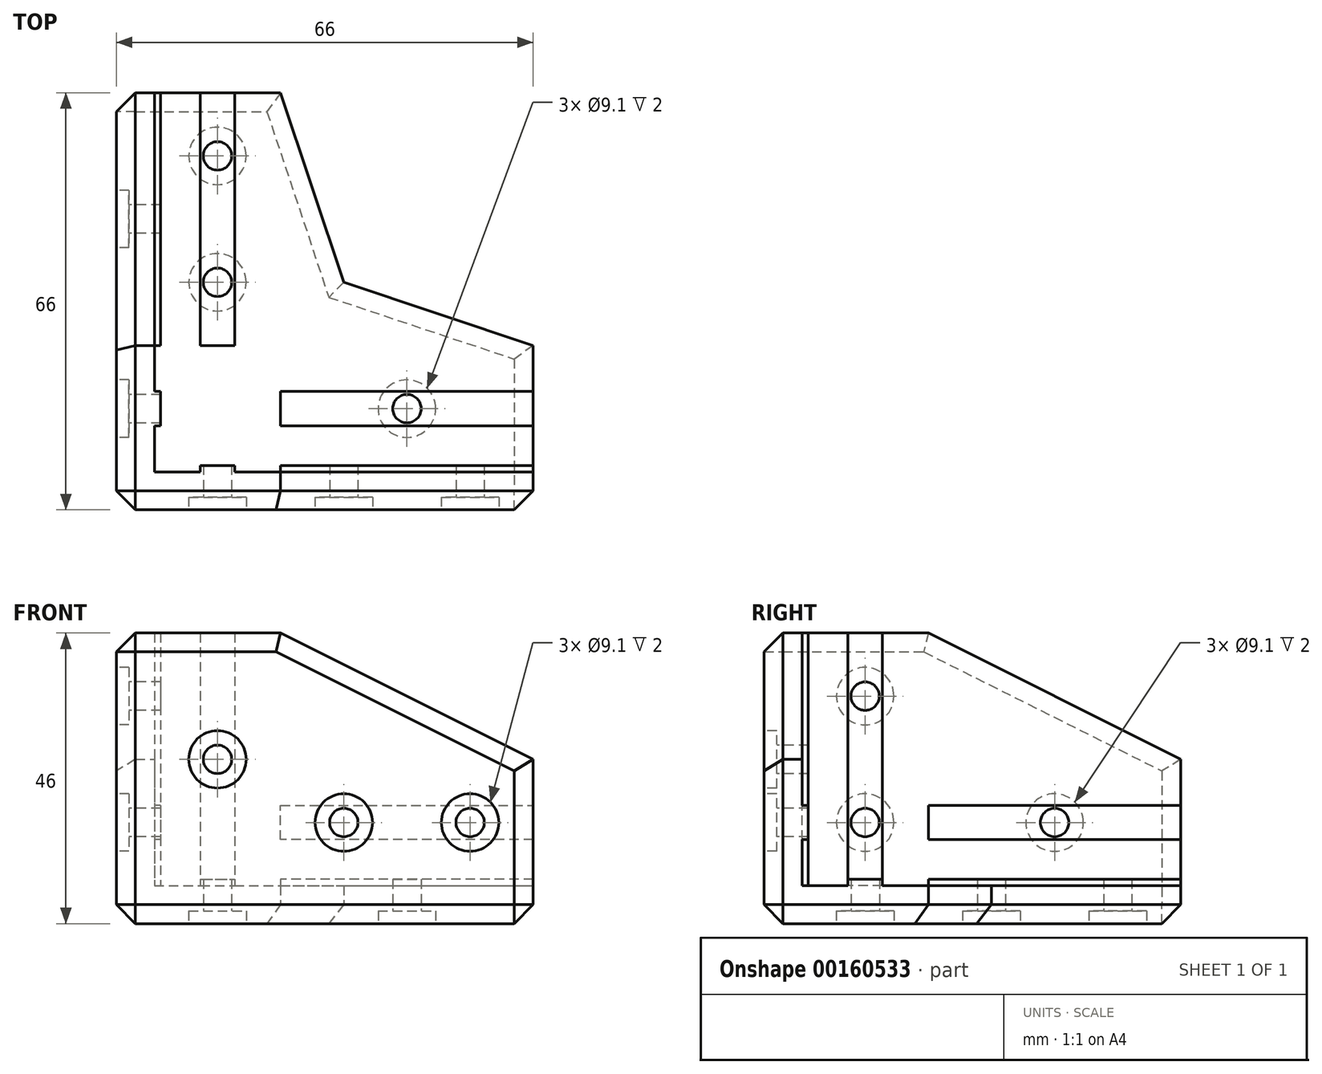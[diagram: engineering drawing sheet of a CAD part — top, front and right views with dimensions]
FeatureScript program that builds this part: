
annotation { "Feature Type Name" : "Feature", "Feature Type Description" : "" }
export const myFeature = defineFeature(function(context is Context, id is Id, definition is map)
    precondition{}
    {
        {
            var Q0;
            Q0=qCreatedBy(makeId("Top.planeOp"),FACE);
            var sketch = newSketch(context, id + "F0", { "sketchPlane" : qUnion([Q0])});
            skLineSegment(sketch, "E0", {"start": v(0, 0) * mm, "end": v(0, 66) * mm});
            skLineSegment(sketch, "E1", {"start": v(0, 66) * mm, "end": v(26, 66) * mm});
            skLineSegment(sketch, "E2", {"start": v(26, 66) * mm, "end": v(26, 26) * mm});
            skLineSegment(sketch, "E3", {"start": v(26, 26) * mm, "end": v(66, 26) * mm});
            skLineSegment(sketch, "E4", {"start": v(66, 26) * mm, "end": v(66, 0) * mm});
            skLineSegment(sketch, "E5", {"start": v(66, 0) * mm, "end": v(0, 0) * mm});
            skLineSegment(sketch, "E6", {"start": v(66, 6) * mm, "end": v(6, 6) * mm, "construction": true});
            skLineSegment(sketch, "E7", {"start": v(6, 6) * mm, "end": v(6, 66) * mm, "construction": true});
            skSolve(sketch);
        }
        {
            var Q0;
            Q0=qSketchRegion(id+"F0",true);
            extrude(context, id + "F1", {"entities" : qUnion([Q0]), "depth" : 6 * mm});
        }
        {
            var Q0;
            Q0=makeQuery(id+"F1.opExtrude","CAP_FACE",FACE,{"disambiguationData":[OSD([sQuery(id+"F0.wireOp",EDGE,"E0"),sQuery(id+"F0.wireOp",EDGE,"E1"),sQuery(id+"F0.wireOp",EDGE,"E2"),sQuery(id+"F0.wireOp",EDGE,"E3"),sQuery(id+"F0.wireOp",EDGE,"E4"),sQuery(id+"F0.wireOp",EDGE,"E5")])],"isStart":false});
            var sketch = newSketch(context, id + "F2", { "sketchPlane" : qUnion([Q0])});
            skLineSegment(sketch, "E8", {"start": v(0, 66) * mm, "end": v(6, 66) * mm});
            skLineSegment(sketch, "E9", {"start": v(6, 66) * mm, "end": v(6, 6) * mm});
            skLineSegment(sketch, "E10", {"start": v(6, 6) * mm, "end": v(66, 6) * mm});
            skLineSegment(sketch, "E11", {"start": v(66, 6) * mm, "end": v(66, 0) * mm});
            skLineSegment(sketch, "E12", {"start": v(66, 0) * mm, "end": v(0, 0) * mm});
            skLineSegment(sketch, "E13", {"start": v(0, 0) * mm, "end": v(0, 66) * mm});
            skSolve(sketch);
        }
        {
            var Q0;
            Q0=makeQuery(id+"F2.imprint","IMPRINT",FACE,{"disambiguationData":[TD([[makeQuery(id+"F2.imprint","IMPRINT",EDGE,{"derivedFrom":sQuery(id+"F2.wireOp",EDGE,"E8")}),-1.0]])]});
            extrude(context, id + "F3", {"entities" : qUnion([Q0]), "operationType" : NewBodyOperationType.ADD, "depth" : 20 * mm});
        }
        {
            var Q0;
            Q0=makeQuery(id+"F3.opExtrude","CAP_FACE",FACE,{"disambiguationData":[OSD([sQuery(id+"F2.wireOp",EDGE,"E8"),sQuery(id+"F2.wireOp",EDGE,"E9"),sQuery(id+"F2.wireOp",EDGE,"E10"),sQuery(id+"F2.wireOp",EDGE,"E11"),sQuery(id+"F2.wireOp",EDGE,"E12"),sQuery(id+"F2.wireOp",EDGE,"E13")])],"isStart":false});
            var sketch = newSketch(context, id + "F4", { "sketchPlane" : qUnion([Q0])});
            skLineSegment(sketch, "E14", {"start": v(6, 26) * mm, "end": v(0, 26) * mm});
            skLineSegment(sketch, "E15", {"start": v(0, 26) * mm, "end": v(0, 0) * mm});
            skLineSegment(sketch, "E16", {"start": v(0, 0) * mm, "end": v(26, 0) * mm});
            skLineSegment(sketch, "E17", {"start": v(26, 0) * mm, "end": v(26, 6) * mm});
            skLineSegment(sketch, "E18", {"start": v(26, 6) * mm, "end": v(6, 6) * mm});
            skLineSegment(sketch, "E19", {"start": v(6, 6) * mm, "end": v(6, 26) * mm});
            skSolve(sketch);
        }
        {
            var Q0;
            Q0=qSketchRegion(id+"F4",true);
            extrude(context, id + "F5", {"entities" : qUnion([Q0]), "operationType" : NewBodyOperationType.ADD, "depth" : 20 * mm});
        }
        {
            var Q0;
            Q0=makeQuery(id+"F1.opExtrude","CAP_FACE",FACE,{"disambiguationData":[OSD([sQuery(id+"F0.wireOp",EDGE,"E0"),sQuery(id+"F0.wireOp",EDGE,"E1"),sQuery(id+"F0.wireOp",EDGE,"E2"),sQuery(id+"F0.wireOp",EDGE,"E3"),sQuery(id+"F0.wireOp",EDGE,"E4"),sQuery(id+"F0.wireOp",EDGE,"E5")])],"isStart":false});
            var sketch = newSketch(context, id + "F6", { "sketchPlane" : qUnion([Q0])});
            skLineSegment(sketch, "E20", {"start": v(66, 16) * mm, "end": v(6, 16) * mm, "construction": true});
            skLineSegment(sketch, "E21", {"start": v(16, 66) * mm, "end": v(16, 6) * mm, "construction": true});
            skLineSegment(sketch, "E22", {"start": v(16, 6) * mm, "end": v(18.71, 6) * mm});
            skLineSegment(sketch, "E23", {"start": v(18.71, 6) * mm, "end": v(18.71, 7) * mm});
            skLineSegment(sketch, "E24", {"start": v(18.71, 7) * mm, "end": v(13.3, 7) * mm});
            skLineSegment(sketch, "E25", {"start": v(13.3, 7) * mm, "end": v(13.3, 6) * mm});
            skLineSegment(sketch, "E26", {"start": v(13.3, 6) * mm, "end": v(16, 6) * mm});
            skLineSegment(sketch, "E27", {"start": v(6, 16) * mm, "end": v(6, 18.7) * mm});
            skLineSegment(sketch, "E28", {"start": v(6, 18.7) * mm, "end": v(7, 18.7) * mm});
            skLineSegment(sketch, "E29", {"start": v(7, 18.7) * mm, "end": v(7, 13.29) * mm});
            skLineSegment(sketch, "E30", {"start": v(7, 13.29) * mm, "end": v(6, 13.29) * mm});
            skLineSegment(sketch, "E31", {"start": v(6, 13.29) * mm, "end": v(6, 16) * mm});
            skSolve(sketch);
        }
        {
            var Q0;
            Q0=qSketchRegion(id+"F6",true);
            extrude(context, id + "F7", {"entities" : qUnion([Q0]), "operationType" : NewBodyOperationType.ADD, "depth" : 40 * mm});
        }
        {
            var Q0;
            Q0=makeQuery(id+"F1.opExtrude","CAP_FACE",FACE,{"disambiguationData":[OSD([sQuery(id+"F0.wireOp",EDGE,"E0"),sQuery(id+"F0.wireOp",EDGE,"E1"),sQuery(id+"F0.wireOp",EDGE,"E2"),sQuery(id+"F0.wireOp",EDGE,"E3"),sQuery(id+"F0.wireOp",EDGE,"E4"),sQuery(id+"F0.wireOp",EDGE,"E5")])],"isStart":false});
            var sketch = newSketch(context, id + "F8", { "sketchPlane" : qUnion([Q0])});
            skLineSegment(sketch, "E32", {"start": v(66, 16) * mm, "end": v(7, 16) * mm, "construction": true});
            skLineSegment(sketch, "E33", {"start": v(66, 16) * mm, "end": v(66, 18.7) * mm});
            skLineSegment(sketch, "E34", {"start": v(66, 18.7) * mm, "end": v(26, 18.7) * mm});
            skLineSegment(sketch, "E35", {"start": v(26, 18.7) * mm, "end": v(26, 13.29) * mm});
            skLineSegment(sketch, "E36", {"start": v(26, 13.29) * mm, "end": v(66, 13.29) * mm});
            skLineSegment(sketch, "E37", {"start": v(66, 13.29) * mm, "end": v(66, 16) * mm});
            skLineSegment(sketch, "E38", {"start": v(16, 66) * mm, "end": v(16, 7) * mm, "construction": true});
            skLineSegment(sketch, "E39", {"start": v(16, 66) * mm, "end": v(13.3, 66) * mm});
            skLineSegment(sketch, "E40", {"start": v(13.3, 66) * mm, "end": v(13.3, 26) * mm});
            skLineSegment(sketch, "E41", {"start": v(13.3, 26) * mm, "end": v(18.7, 26) * mm});
            skLineSegment(sketch, "E42", {"start": v(18.7, 26) * mm, "end": v(18.7, 66) * mm});
            skLineSegment(sketch, "E43", {"start": v(18.7, 66) * mm, "end": v(16, 66) * mm});
            skSolve(sketch);
        }
        {
            var Q0;
            Q0=qSketchRegion(id+"F8",true);
            extrude(context, id + "F9", {"entities" : qUnion([Q0]), "operationType" : NewBodyOperationType.ADD, "flatOperationType" : FlatOperationType.REMOVE, "offsetDistance" : 25 * mm, "depth" : 1 * mm, "domain" : OperationDomain.MODEL});
        }
        {
            var Q0;
            {var subQ1=sQuery(id+"F2.wireOp",EDGE,"E10");var subQ2=sQuery(id+"F0.wireOp",EDGE,"E4");var subQ3=sQuery(id+"F4.wireOp",EDGE,"E18");Q0=makeQuery(id+"F7.boolean.opBoolean","SPLIT",FACE,{"disambiguationData":[TD([makeQuery(id+"F1.opExtrude","SWEPT_FACE",FACE,{"disambiguationData":[OSD([subQ2])]})])],"derivedFrom":makeQuery(id+"F5.boolean.opBoolean","MERGE",FACE,{"derivedFrom":[makeQuery(id+"F3.opExtrude","SWEPT_FACE",FACE,{"disambiguationData":[OSD([subQ1])]}),makeQuery(id+"F5.opExtrude","SWEPT_FACE",FACE,{"disambiguationData":[OSD([subQ3])]})]})});}
            var sketch = newSketch(context, id + "F10", { "sketchPlane" : qUnion([Q0])});
            skLineSegment(sketch, "E44", {"start": v(-66, 16) * mm, "end": v(-26, 16) * mm, "construction": true});
            skLineSegment(sketch, "E45", {"start": v(-66, 16) * mm, "end": v(-66, 13.3) * mm});
            skLineSegment(sketch, "E46", {"start": v(-66, 13.3) * mm, "end": v(-26, 13.3) * mm});
            skLineSegment(sketch, "E47", {"start": v(-26, 13.3) * mm, "end": v(-26, 16) * mm});
            skLineSegment(sketch, "E48", {"start": v(-26, 18.71) * mm, "end": v(-66, 18.71) * mm});
            skLineSegment(sketch, "E49", {"start": v(-66, 18.71) * mm, "end": v(-66, 16) * mm});
            skLineSegment(sketch, "E50", {"start": v(-26, 18.71) * mm, "end": v(-26, 16) * mm});
            skSolve(sketch);
        }
        {
            var Q0;
            Q0=qSketchRegion(id+"F10",true);
            extrude(context, id + "F11", {"entities" : qUnion([Q0]), "operationType" : NewBodyOperationType.ADD, "flatOperationType" : FlatOperationType.REMOVE, "offsetDistance" : 25 * mm, "depth" : 1 * mm, "domain" : OperationDomain.MODEL});
        }
        {
            var Q0;
            {var subQ0=sQuery(id+"F2.wireOp",EDGE,"E9");var subQ3=sQuery(id+"F0.wireOp",EDGE,"E1");var subQ5=sQuery(id+"F4.wireOp",EDGE,"E19");Q0=makeQuery(id+"F7.boolean.opBoolean","SPLIT",FACE,{"disambiguationData":[TD([makeQuery(id+"F1.opExtrude","SWEPT_FACE",FACE,{"disambiguationData":[OSD([subQ3])]})])],"derivedFrom":makeQuery(id+"F5.boolean.opBoolean","MERGE",FACE,{"derivedFrom":[makeQuery(id+"F3.opExtrude","SWEPT_FACE",FACE,{"disambiguationData":[OSD([subQ0])]}),makeQuery(id+"F5.opExtrude","SWEPT_FACE",FACE,{"disambiguationData":[OSD([subQ5])]})]})});}
            var sketch = newSketch(context, id + "F12", { "sketchPlane" : qUnion([Q0])});
            skLineSegment(sketch, "E51", {"start": v(66, 16) * mm, "end": v(26, 16) * mm, "construction": true});
            skLineSegment(sketch, "E52", {"start": v(66, 16) * mm, "end": v(66, 18.71) * mm});
            skLineSegment(sketch, "E53", {"start": v(66, 18.71) * mm, "end": v(26, 18.7) * mm});
            skLineSegment(sketch, "E54", {"start": v(26, 18.7) * mm, "end": v(26, 13.29) * mm});
            skLineSegment(sketch, "E55", {"start": v(26, 13.29) * mm, "end": v(66, 13.29) * mm});
            skLineSegment(sketch, "E56", {"start": v(66, 16) * mm, "end": v(66, 13.29) * mm});
            skSolve(sketch);
        }
        {
            var Q0;
            Q0=qSketchRegion(id+"F12",true);
            extrude(context, id + "F13", {"entities" : qUnion([Q0]), "operationType" : NewBodyOperationType.ADD, "flatOperationType" : FlatOperationType.REMOVE, "offsetDistance" : 25 * mm, "depth" : 1 * mm, "domain" : OperationDomain.MODEL});
        }
        {
            var Q0;
            Q0=makeQuery(id+"F5.boolean.opBoolean","MERGE",FACE,{"derivedFrom":[makeQuery(id+"F3.boolean.opBoolean","MERGE",FACE,{"derivedFrom":[makeQuery(id+"F1.opExtrude","SWEPT_FACE",FACE,{"disambiguationData":[OSD([sQuery(id+"F0.wireOp",EDGE,"E5")])]}),makeQuery(id+"F3.opExtrude","SWEPT_FACE",FACE,{"disambiguationData":[OSD([sQuery(id+"F2.wireOp",EDGE,"E12")])]})]}),makeQuery(id+"F5.opExtrude","SWEPT_FACE",FACE,{"disambiguationData":[OSD([sQuery(id+"F4.wireOp",EDGE,"E16")])]})]});
            var sketch = newSketch(context, id + "F14", { "sketchPlane" : qUnion([Q0])});
            skLineSegment(sketch, "E57", {"start": v(6, 46) * mm, "end": v(6, 6) * mm, "construction": true});
            skLineSegment(sketch, "E58", {"start": v(6, 6) * mm, "end": v(66, 6) * mm, "construction": true});
            skCircle(sketch, "E59", {"center": v(56, 16) * mm, "radius": 2.25 * mm});
            skCircle(sketch, "E60", {"center": v(36, 16) * mm, "radius": 2.25 * mm});
            skCircle(sketch, "E61", {"center": v(16, 26) * mm, "radius": 2.25 * mm});
            skLineSegment(sketch, "E62", {"start": v(26, 26) * mm, "end": v(6, 26) * mm, "construction": true});
            skLineSegment(sketch, "E63", {"start": v(26, 26) * mm, "end": v(26, 6) * mm, "construction": true});
            skSolve(sketch);
        }
        {
            var Q0;
            Q0=makeQuery(id+"F14.imprint","IMPRINT",FACE,{"disambiguationData":[TD([[makeQuery(id+"F14.imprint","IMPRINT",EDGE,{"derivedFrom":sQuery(id+"F14.wireOp",EDGE,"E59")}),1.0]])]});
            var Q1;
            Q1=makeQuery(id+"F14.imprint","IMPRINT",FACE,{"disambiguationData":[TD([[makeQuery(id+"F14.imprint","IMPRINT",EDGE,{"derivedFrom":sQuery(id+"F14.wireOp",EDGE,"E61")}),1.0]])]});
            var Q2;
            Q2=makeQuery(id+"F14.imprint","IMPRINT",FACE,{"disambiguationData":[TD([[makeQuery(id+"F14.imprint","IMPRINT",EDGE,{"derivedFrom":sQuery(id+"F14.wireOp",EDGE,"E60")}),1.0]])]});
            extrude(context, id + "F15", {"entities" : qUnion([Q0, Q1, Q2]), "operationType" : NewBodyOperationType.REMOVE, "endBound" : BoundingType.UP_TO_NEXT, "oppositeDirection" : true, "depth" : 25 * mm});
        }
        {
            var Q0;
            Q0=makeQuery(id+"F5.boolean.opBoolean","MERGE",FACE,{"derivedFrom":[makeQuery(id+"F3.boolean.opBoolean","MERGE",FACE,{"derivedFrom":[makeQuery(id+"F1.opExtrude","SWEPT_FACE",FACE,{"disambiguationData":[OSD([sQuery(id+"F0.wireOp",EDGE,"E0")])]}),makeQuery(id+"F3.opExtrude","SWEPT_FACE",FACE,{"disambiguationData":[OSD([sQuery(id+"F2.wireOp",EDGE,"E13")])]})]}),makeQuery(id+"F5.opExtrude","SWEPT_FACE",FACE,{"disambiguationData":[OSD([sQuery(id+"F4.wireOp",EDGE,"E15")])]})]});
            var sketch = newSketch(context, id + "F16", { "sketchPlane" : qUnion([Q0])});
            skLineSegment(sketch, "E64", {"start": v(-6, 46) * mm, "end": v(-6, 6) * mm, "construction": true});
            skLineSegment(sketch, "E65", {"start": v(-6, 6) * mm, "end": v(-66, 6) * mm, "construction": true});
            skCircle(sketch, "E66", {"center": v(-16, 36) * mm, "radius": 2.25 * mm});
            skCircle(sketch, "E67", {"center": v(-46, 16) * mm, "radius": 2.25 * mm});
            skCircle(sketch, "E68", {"center": v(-16, 16) * mm, "radius": 2.25 * mm});
            skSolve(sketch);
        }
        {
            var Q0;
            Q0=qSketchRegion(id+"F16",true);
            extrude(context, id + "F17", {"entities" : qUnion([Q0]), "operationType" : NewBodyOperationType.REMOVE, "endBound" : BoundingType.UP_TO_NEXT, "oppositeDirection" : true, "depth" : 25 * mm});
        }
        {
            var Q0;
            Q0=makeQuery(id+"F1.opExtrude","CAP_FACE",FACE,{"disambiguationData":[OSD([sQuery(id+"F0.wireOp",EDGE,"E0"),sQuery(id+"F0.wireOp",EDGE,"E1"),sQuery(id+"F0.wireOp",EDGE,"E2"),sQuery(id+"F0.wireOp",EDGE,"E3"),sQuery(id+"F0.wireOp",EDGE,"E4"),sQuery(id+"F0.wireOp",EDGE,"E5")])],"isStart":true});
            var sketch = newSketch(context, id + "F18", { "sketchPlane" : qUnion([Q0])});
            skLineSegment(sketch, "E69", {"start": v(66, -6) * mm, "end": v(6, -6) * mm, "construction": true});
            skLineSegment(sketch, "E70", {"start": v(6, -6) * mm, "end": v(6, -66) * mm, "construction": true});
            skCircle(sketch, "E71", {"center": v(46, -16) * mm, "radius": 2.25 * mm});
            skCircle(sketch, "E72", {"center": v(16, -56) * mm, "radius": 2.25 * mm});
            skCircle(sketch, "E73", {"center": v(16, -36) * mm, "radius": 2.25 * mm});
            skSolve(sketch);
        }
        {
            var Q0;
            Q0=qSketchRegion(id+"F18",true);
            extrude(context, id + "F19", {"entities" : qUnion([Q0]), "operationType" : NewBodyOperationType.REMOVE, "endBound" : BoundingType.UP_TO_NEXT, "oppositeDirection" : true, "depth" : 25 * mm});
        }
        {
            var Q0;
            Q0=makeQuery(id+"F5.boolean.opBoolean","MERGE",FACE,{"derivedFrom":[makeQuery(id+"F3.boolean.opBoolean","MERGE",FACE,{"derivedFrom":[makeQuery(id+"F1.opExtrude","SWEPT_FACE",FACE,{"disambiguationData":[OSD([sQuery(id+"F0.wireOp",EDGE,"E5")])]}),makeQuery(id+"F3.opExtrude","SWEPT_FACE",FACE,{"disambiguationData":[OSD([sQuery(id+"F2.wireOp",EDGE,"E12")])]})]}),makeQuery(id+"F5.opExtrude","SWEPT_FACE",FACE,{"disambiguationData":[OSD([sQuery(id+"F4.wireOp",EDGE,"E16")])]})]});
            var sketch = newSketch(context, id + "F20", { "sketchPlane" : qUnion([Q0])});
            skCircle(sketch, "E74", {"center": v(16, 26) * mm, "radius": 4.55 * mm});
            skCircle(sketch, "E75", {"center": v(36, 16) * mm, "radius": 4.55 * mm});
            skCircle(sketch, "E76", {"center": v(56, 16) * mm, "radius": 4.55 * mm});
            skSolve(sketch);
        }
        {
            var Q0;
            Q0=qSketchRegion(id+"F20",true);
            extrude(context, id + "F21", {"entities" : qUnion([Q0]), "operationType" : NewBodyOperationType.REMOVE, "oppositeDirection" : true, "depth" : 2 * mm});
        }
        {
            var Q0;
            Q0=makeQuery(id+"F5.boolean.opBoolean","MERGE",FACE,{"derivedFrom":[makeQuery(id+"F3.boolean.opBoolean","MERGE",FACE,{"derivedFrom":[makeQuery(id+"F1.opExtrude","SWEPT_FACE",FACE,{"disambiguationData":[OSD([sQuery(id+"F0.wireOp",EDGE,"E0")])]}),makeQuery(id+"F3.opExtrude","SWEPT_FACE",FACE,{"disambiguationData":[OSD([sQuery(id+"F2.wireOp",EDGE,"E13")])]})]}),makeQuery(id+"F5.opExtrude","SWEPT_FACE",FACE,{"disambiguationData":[OSD([sQuery(id+"F4.wireOp",EDGE,"E15")])]})]});
            var sketch = newSketch(context, id + "F22", { "sketchPlane" : qUnion([Q0])});
            skCircle(sketch, "E77", {"center": v(-16, 36) * mm, "radius": 4.55 * mm});
            skCircle(sketch, "E78", {"center": v(-46, 16) * mm, "radius": 4.55 * mm});
            skCircle(sketch, "E79", {"center": v(-16, 16) * mm, "radius": 4.55 * mm});
            skSolve(sketch);
        }
        {
            var Q0;
            Q0=qSketchRegion(id+"F22",true);
            extrude(context, id + "F23", {"entities" : qUnion([Q0]), "operationType" : NewBodyOperationType.REMOVE, "oppositeDirection" : true, "depth" : 2 * mm});
        }
        {
            var Q0;
            Q0=makeQuery(id+"F1.opExtrude","CAP_FACE",FACE,{"disambiguationData":[OSD([sQuery(id+"F0.wireOp",EDGE,"E0"),sQuery(id+"F0.wireOp",EDGE,"E1"),sQuery(id+"F0.wireOp",EDGE,"E2"),sQuery(id+"F0.wireOp",EDGE,"E3"),sQuery(id+"F0.wireOp",EDGE,"E4"),sQuery(id+"F0.wireOp",EDGE,"E5")])],"isStart":true});
            var sketch = newSketch(context, id + "F24", { "sketchPlane" : qUnion([Q0])});
            skCircle(sketch, "E80", {"center": v(16, -56) * mm, "radius": 4.55 * mm});
            skCircle(sketch, "E81", {"center": v(46, -16) * mm, "radius": 4.55 * mm});
            skCircle(sketch, "E82", {"center": v(16, -36) * mm, "radius": 4.55 * mm});
            skSolve(sketch);
        }
        {
            var Q0;
            Q0=qSketchRegion(id+"F24",true);
            extrude(context, id + "F25", {"entities" : qUnion([Q0]), "operationType" : NewBodyOperationType.REMOVE, "oppositeDirection" : true, "depth" : 2 * mm});
        }
        {
            var Q0;
            Q0=makeQuery(id+"F5.boolean.opBoolean","MERGE",FACE,{"derivedFrom":[makeQuery(id+"F3.boolean.opBoolean","MERGE",FACE,{"derivedFrom":[makeQuery(id+"F1.opExtrude","SWEPT_FACE",FACE,{"disambiguationData":[OSD([sQuery(id+"F0.wireOp",EDGE,"E5")])]}),makeQuery(id+"F3.opExtrude","SWEPT_FACE",FACE,{"disambiguationData":[OSD([sQuery(id+"F2.wireOp",EDGE,"E12")])]})]}),makeQuery(id+"F5.opExtrude","SWEPT_FACE",FACE,{"disambiguationData":[OSD([sQuery(id+"F4.wireOp",EDGE,"E16")])]})]});
            var sketch = newSketch(context, id + "F26", { "sketchPlane" : qUnion([Q0])});
            skLineSegment(sketch, "E83", {"start": v(26, 46) * mm, "end": v(26, 26) * mm});
            skLineSegment(sketch, "E84", {"start": v(26, 26) * mm, "end": v(66, 26) * mm});
            skLineSegment(sketch, "E85", {"start": v(66, 26) * mm, "end": v(26, 46) * mm});
            skSolve(sketch);
        }
        {
            var Q0;
            Q0 = qSketchRegion(id + "F26", true);
            extrude(context, id + "F27", {"entities" : qUnion([Q0]), "operationType" : NewBodyOperationType.ADD, "oppositeDirection" : true, "depth" : 6 * mm});
        }
        {
            var Q0;
            Q0=makeQuery(id+"F5.boolean.opBoolean","MERGE",FACE,{"derivedFrom":[makeQuery(id+"F3.boolean.opBoolean","MERGE",FACE,{"derivedFrom":[makeQuery(id+"F1.opExtrude","SWEPT_FACE",FACE,{"disambiguationData":[OSD([sQuery(id+"F0.wireOp",EDGE,"E0")])]}),makeQuery(id+"F3.opExtrude","SWEPT_FACE",FACE,{"disambiguationData":[OSD([sQuery(id+"F2.wireOp",EDGE,"E13")])]})]}),makeQuery(id+"F5.opExtrude","SWEPT_FACE",FACE,{"disambiguationData":[OSD([sQuery(id+"F4.wireOp",EDGE,"E15")])]})]});
            var sketch = newSketch(context, id + "F28", { "sketchPlane" : qUnion([Q0])});
            skLineSegment(sketch, "E86", {"start": v(-66, 26) * mm, "end": v(-26, 26) * mm});
            skLineSegment(sketch, "E87", {"start": v(-26, 26) * mm, "end": v(-26, 46) * mm});
            skLineSegment(sketch, "E88", {"start": v(-26, 46) * mm, "end": v(-66, 26) * mm});
            skSolve(sketch);
        }
        {
            var Q0;
            Q0 = qSketchRegion(id + "F28", true);
            extrude(context, id + "F29", {"entities" : qUnion([Q0]), "operationType" : NewBodyOperationType.ADD, "oppositeDirection" : true, "depth" : 6 * mm});
        }
        {
            var Q0;
            Q0=makeQuery(id+"F1.opExtrude","CAP_FACE",FACE,{"disambiguationData":[OSD([sQuery(id+"F0.wireOp",EDGE,"E0"),sQuery(id+"F0.wireOp",EDGE,"E1"),sQuery(id+"F0.wireOp",EDGE,"E2"),sQuery(id+"F0.wireOp",EDGE,"E3"),sQuery(id+"F0.wireOp",EDGE,"E4"),sQuery(id+"F0.wireOp",EDGE,"E5")])],"isStart":true});
            var sketch = newSketch(context, id + "F30", { "sketchPlane" : qUnion([Q0])});
            skLineSegment(sketch, "E89", {"start": v(26, -66) * mm, "end": v(26, -26) * mm});
            skLineSegment(sketch, "E90", {"start": v(26, -26) * mm, "end": v(66, -26) * mm});
            skLineSegment(sketch, "E91", {"start": v(26, -36) * mm, "end": v(36, -36) * mm, "construction": true});
            skLineSegment(sketch, "E92", {"start": v(36, -36) * mm, "end": v(36, -26) * mm, "construction": true});
            skLineSegment(sketch, "E93", {"start": v(26, -66) * mm, "end": v(36, -36) * mm});
            skLineSegment(sketch, "E94", {"start": v(36, -36) * mm, "end": v(66, -26) * mm});
            skSolve(sketch);
        }
        {
            var Q0;
            Q0 = qSketchRegion(id + "F30", true);
            extrude(context, id + "F31", {"entities" : qUnion([Q0]), "operationType" : NewBodyOperationType.ADD, "oppositeDirection" : true, "depth" : 6 * mm});
        }
        {
            var Q0;
            Q0=makeQuery(id+"F27.opExtrude","CAP_EDGE",EDGE,{"disambiguationData":[OSD([sQuery(id+"F26.wireOp",EDGE,"E85")])],"isStart":true});
            var Q1;
            Q1=makeQuery(id+"F5.opExtrude","CAP_EDGE",EDGE,{"disambiguationData":[OSD([sQuery(id+"F4.wireOp",EDGE,"E16")])],"isStart":false});
            var Q2;
            Q2=makeQuery(id+"F5.opExtrude","CAP_EDGE",EDGE,{"disambiguationData":[OSD([sQuery(id+"F4.wireOp",EDGE,"E15")])],"isStart":false});
            var Q3;
            Q3=makeQuery(id+"F29.opExtrude","CAP_EDGE",EDGE,{"disambiguationData":[OSD([sQuery(id+"F28.wireOp",EDGE,"E88")])],"isStart":true});
            var Q4;
            Q4=makeQuery(id+"F31.opExtrude","CAP_EDGE",EDGE,{"disambiguationData":[OSD([sQuery(id+"F30.wireOp",EDGE,"E93")])],"isStart":true});
            var Q5;
            Q5=makeQuery(id+"F31.opExtrude","CAP_EDGE",EDGE,{"disambiguationData":[OSD([sQuery(id+"F30.wireOp",EDGE,"E94")])],"isStart":true});
            var Q6;
            Q6=makeQuery(id+"F1.opExtrude","CAP_EDGE",EDGE,{"disambiguationData":[OSD([sQuery(id+"F0.wireOp",EDGE,"E1")])],"isStart":true});
            var Q7;
            Q7=makeQuery(id+"F1.opExtrude","CAP_EDGE",EDGE,{"disambiguationData":[OSD([sQuery(id+"F0.wireOp",EDGE,"E4")])],"isStart":true});
            var Q8;
            Q8=makeQuery(id+"F3.boolean.opBoolean","MERGE",EDGE,{"derivedFrom":[makeQuery(id+"F1.opExtrude","SWEPT_EDGE",EDGE,{"disambiguationData":[OSD([sQuery(id+"F0.wireOp",EDGE,"E4"),sQuery(id+"F0.wireOp",EDGE,"E5")])]}),makeQuery(id+"F3.opExtrude","SWEPT_EDGE",EDGE,{"disambiguationData":[OSD([sQuery(id+"F2.wireOp",EDGE,"E11"),sQuery(id+"F2.wireOp",EDGE,"E12")])]})]});
            var Q9;
            Q9=makeQuery(id+"F3.boolean.opBoolean","MERGE",EDGE,{"derivedFrom":[makeQuery(id+"F1.opExtrude","SWEPT_EDGE",EDGE,{"disambiguationData":[OSD([sQuery(id+"F0.wireOp",EDGE,"E0"),sQuery(id+"F0.wireOp",EDGE,"E1")])]}),makeQuery(id+"F3.opExtrude","SWEPT_EDGE",EDGE,{"disambiguationData":[OSD([sQuery(id+"F2.wireOp",EDGE,"E8"),sQuery(id+"F2.wireOp",EDGE,"E13")])]})]});
            var Q10;
            Q10=makeQuery(id+"F1.opExtrude","CAP_EDGE",EDGE,{"disambiguationData":[OSD([sQuery(id+"F0.wireOp",EDGE,"E5")])],"isStart":true});
            var Q11;
            Q11=makeQuery(id+"F1.opExtrude","CAP_EDGE",EDGE,{"disambiguationData":[OSD([sQuery(id+"F0.wireOp",EDGE,"E0")])],"isStart":true});
            var Q12;
            Q12=makeQuery(id+"F5.boolean.opBoolean","MERGE",EDGE,{"derivedFrom":[makeQuery(id+"F3.boolean.opBoolean","MERGE",EDGE,{"derivedFrom":[makeQuery(id+"F1.opExtrude","SWEPT_EDGE",EDGE,{"disambiguationData":[OSD([sQuery(id+"F0.wireOp",EDGE,"E0"),sQuery(id+"F0.wireOp",EDGE,"E5")])]}),makeQuery(id+"F3.opExtrude","SWEPT_EDGE",EDGE,{"disambiguationData":[OSD([sQuery(id+"F2.wireOp",EDGE,"E12"),sQuery(id+"F2.wireOp",EDGE,"E13")])]})]}),makeQuery(id+"F5.opExtrude","SWEPT_EDGE",EDGE,{"disambiguationData":[OSD([sQuery(id+"F4.wireOp",EDGE,"E15"),sQuery(id+"F4.wireOp",EDGE,"E16")])]})]});
            chamfer(context, id + "F32", {"entities" : qUnion([Q0, Q1, Q2, Q3, Q4, Q5, Q6, Q7, Q8, Q9, Q10, Q11, Q12]), "width" : 3 * mm, "tangentPropagation" : true});
        }
    });
